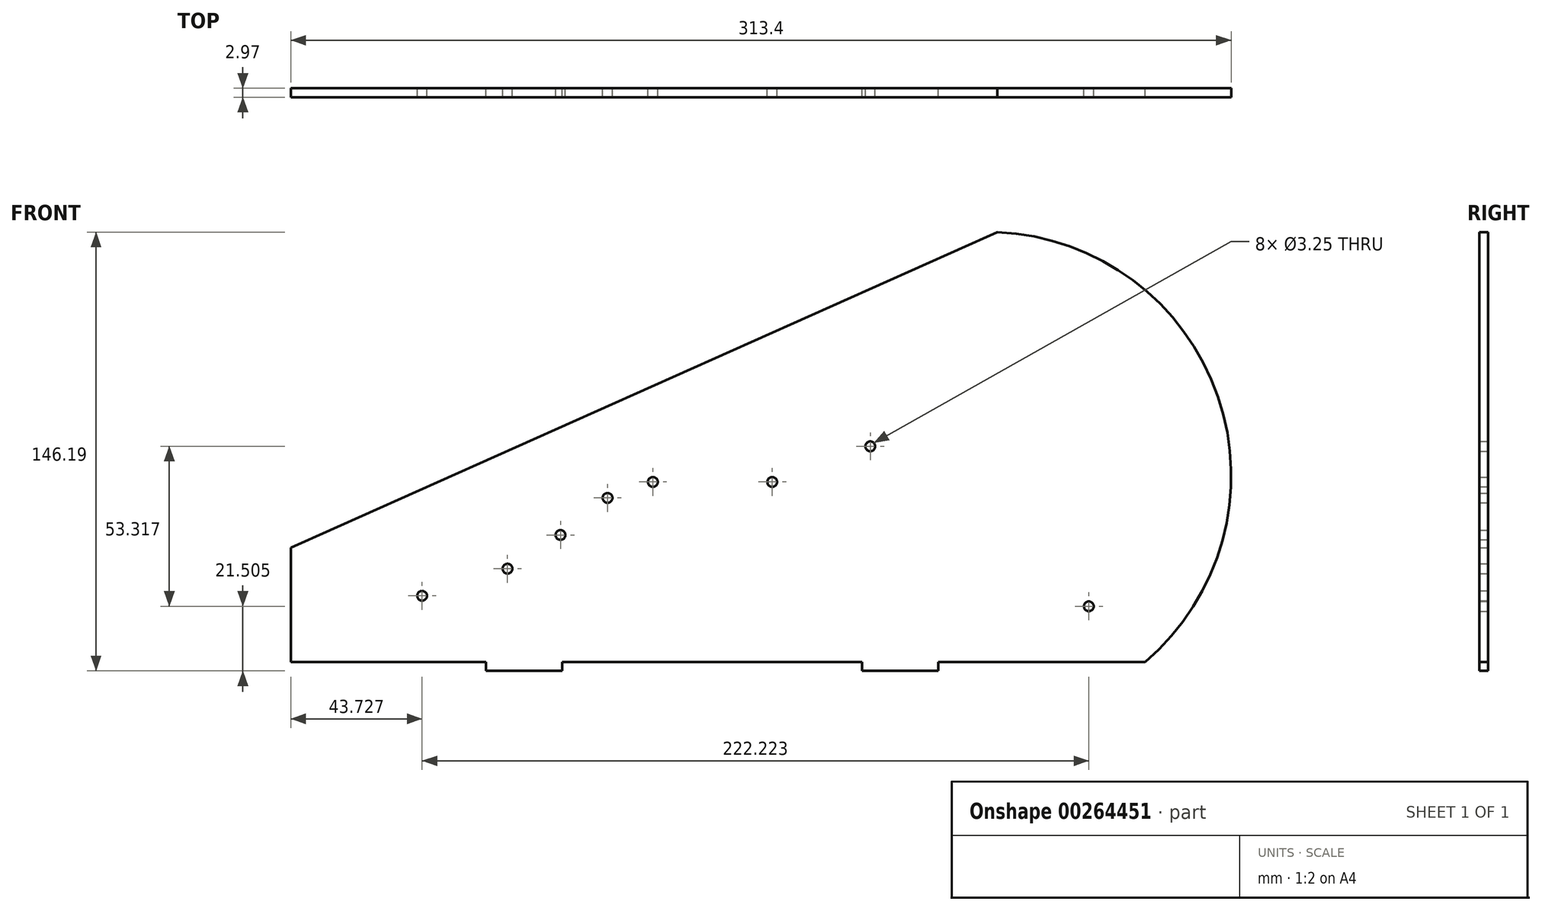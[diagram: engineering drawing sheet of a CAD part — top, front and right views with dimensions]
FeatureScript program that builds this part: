
annotation { "Feature Type Name" : "Feature", "Feature Type Description" : "" }
export const myFeature = defineFeature(function(context is Context, id is Id, definition is map)
    precondition{}
    {
        {
            var Q0;
            Q0=qCreatedBy(makeId("Front.planeOp"),FACE);
            var sketch = newSketch(context, id + "F0", { "sketchPlane" : qUnion([Q0])});
            skCircle(sketch, "E0", {"center": v(218.51, 73.43) * mm, "radius": 1.63 * mm});
            skPoint(sketch, "E1.orphan", {"position": v(-70.07, -28.14) * mm});
            skLineSegment(sketch, "E2", {"start": v(218.51, 73.43) * mm, "end": v(185.83, 61.56) * mm});
            skCircle(sketch, "E3", {"center": v(185.83, 61.56) * mm, "radius": 1.63 * mm});
            skLineSegment(sketch, "E4", {"start": v(185.83, 61.56) * mm, "end": v(146.05, 61.56) * mm});
            skCircle(sketch, "E5", {"center": v(146.05, 61.56) * mm, "radius": 1.63 * mm});
            skPoint(sketch, "E6.end.orphan", {"position": v(56.03, 61.56) * mm});
            skLineSegment(sketch, "E7", {"start": v(146.05, 61.56) * mm, "end": v(130.94, 56.24) * mm});
            skLineSegment(sketch, "E8", {"start": v(130.94, 56.24) * mm, "end": v(115.26, 43.88) * mm});
            skLineSegment(sketch, "E9", {"start": v(115.26, 43.88) * mm, "end": v(97.6, 32.65) * mm});
            skLineSegment(sketch, "E10", {"start": v(97.6, 32.65) * mm, "end": v(69.13, 23.61) * mm});
            skCircle(sketch, "E11", {"center": v(130.94, 56.24) * mm, "radius": 1.63 * mm});
            skCircle(sketch, "E12", {"center": v(69.13, 23.61) * mm, "radius": 1.63 * mm});
            skCircle(sketch, "E13", {"center": v(97.6, 32.65) * mm, "radius": 1.63 * mm});
            skCircle(sketch, "E14", {"center": v(115.26, 43.88) * mm, "radius": 1.63 * mm});
            skPoint(sketch, "E15.orphan", {"position": v(330.2, -28.14) * mm});
            skPoint(sketch, "E16.start.orphan", {"position": v(0, 175.06) * mm});
            skArc(sketch, "E17", {"start": v(144.74, 62.52) * mm, "mid": v(144.77, 61.52) * mm, "end": v(144.8, 60.52) * mm});
            skPoint(sketch, "E18.orphan", {"position": v(273.03, 150.1) * mm});
            skLineSegment(sketch, "E19", {"start": v(25.4, 39.68) * mm, "end": v(25.4, 1.58) * mm});
            skLineSegment(sketch, "E20", {"start": v(25.4, 39.68) * mm, "end": v(260.9, 144.8) * mm});
            skArc(sketch, "E21", {"start": v(310.1, 1.58) * mm, "mid": v(334.39, 89.99) * mm, "end": v(260.9, 144.8) * mm});
            skPoint(sketch, "E22.orphan", {"position": v(284.56, -5.7) * mm});
            skPoint(sketch, "E23.center.orphan", {"position": v(273.03, 121.04) * mm});
            skPoint(sketch, "E23.start.orphan", {"position": v(280.35, 146.7) * mm});
            skLineSegment(sketch, "E24", {"start": v(25.4, 1.58) * mm, "end": v(90.47, 1.58) * mm});
            skLineSegment(sketch, "E25", {"start": v(90.47, 1.58) * mm, "end": v(90.47, -1.4) * mm});
            skLineSegment(sketch, "E26", {"start": v(90.47, -1.4) * mm, "end": v(115.87, -1.4) * mm});
            skLineSegment(sketch, "E27", {"start": v(115.87, -1.4) * mm, "end": v(115.87, 1.58) * mm});
            skLineSegment(sketch, "E28", {"start": v(215.81, 1.58) * mm, "end": v(215.81, -1.4) * mm});
            skLineSegment(sketch, "E29", {"start": v(215.81, -1.4) * mm, "end": v(241.23, -1.4) * mm});
            skPoint(sketch, "E30.end.orphan", {"position": v(246.64, 0) * mm});
            skLineSegment(sketch, "E31", {"start": v(241.23, -1.4) * mm, "end": v(241.23, 1.58) * mm});
            skLineSegment(sketch, "E32.trimOffspring", {"start": v(115.87, 1.58) * mm, "end": v(215.81, 1.58) * mm});
            skLineSegment(sketch, "E33.trimOffspring", {"start": v(241.23, 1.58) * mm, "end": v(310.1, 1.58) * mm});
            skPoint(sketch, "E34.center.orphan", {"position": v(284.56, 9.36) * mm});
            skCircle(sketch, "E35", {"center": v(291.35, 20.12) * mm, "radius": 1.63 * mm});
            skSolve(sketch);
        }
        {
            var Q0;
            Q0 = qSketchRegion(id + "F0", true);
            extrude(context, id + "F1", {"entities" : qUnion([Q0]), "depth" : 2.97 * mm});
        }
    });
